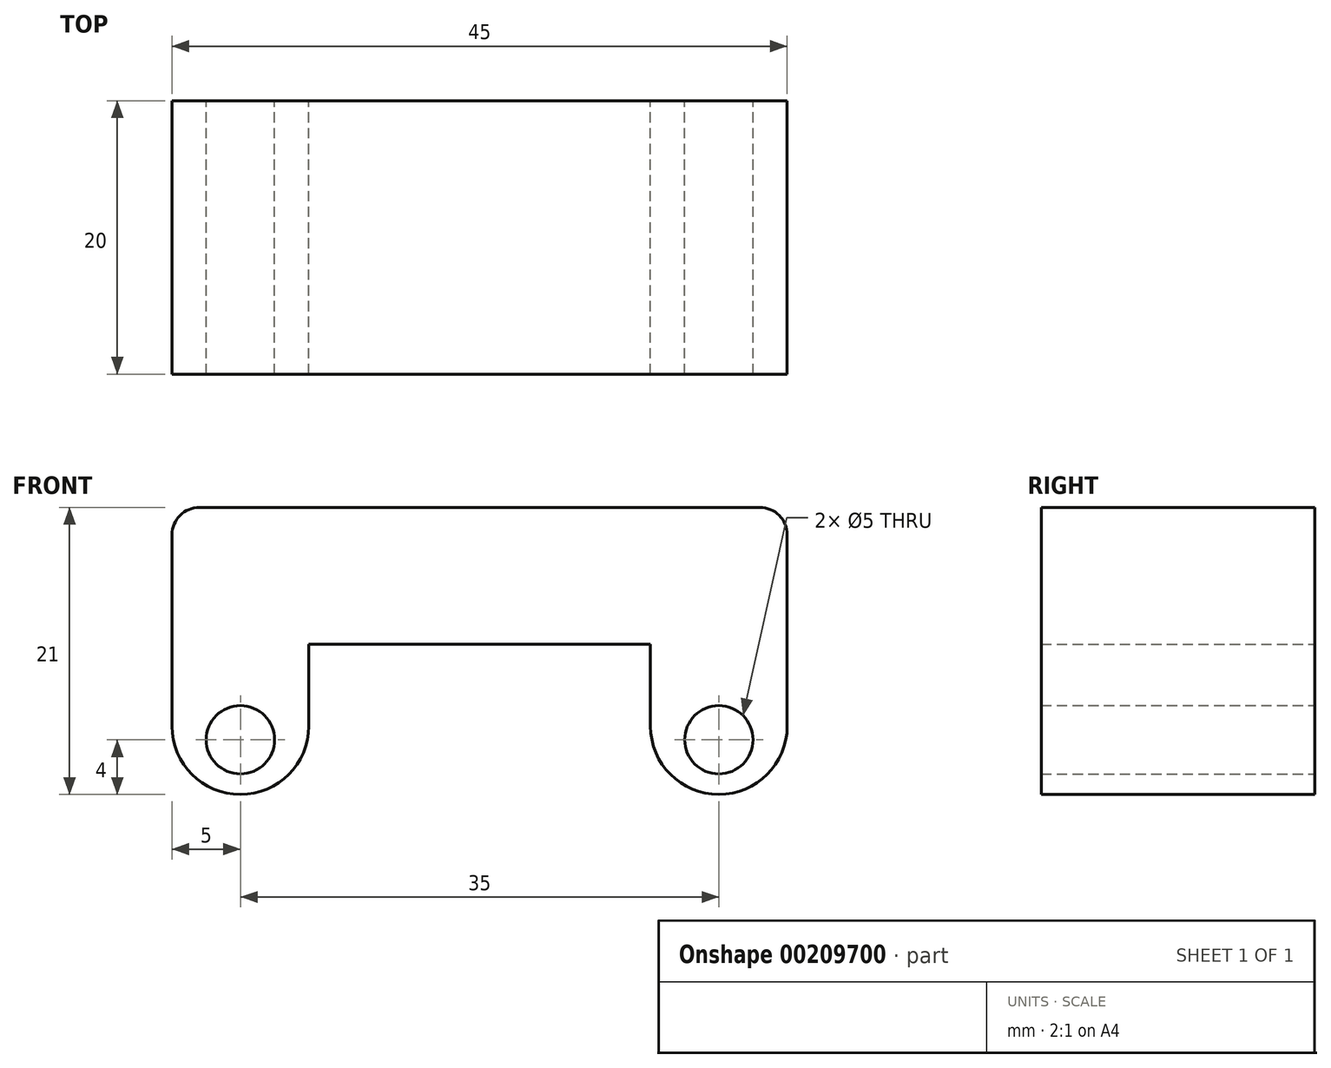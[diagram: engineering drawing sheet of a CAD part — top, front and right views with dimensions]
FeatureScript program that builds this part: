
annotation { "Feature Type Name" : "Feature", "Feature Type Description" : "" }
export const myFeature = defineFeature(function(context is Context, id is Id, definition is map)
    precondition{}
    {
        {
            var Q0;
            Q0=qCreatedBy(makeId("Front.planeOp"),FACE);
            var sketch = newSketch(context, id + "F0", { "sketchPlane" : qUnion([Q0])});
            skLineSegment(sketch, "E0.bottom", {"start": v(-22.5, 10.5) * mm, "end": v(22.5, 10.5) * mm});
            skLineSegment(sketch, "E0.top", {"start": v(-22.5, -10.5) * mm, "end": v(22.5, -10.5) * mm});
            skLineSegment(sketch, "E0.left", {"start": v(-22.5, 10.5) * mm, "end": v(-22.5, -10.5) * mm});
            skLineSegment(sketch, "E0.right", {"start": v(22.5, 10.5) * mm, "end": v(22.5, -10.5) * mm});
            skPoint(sketch, "E0.middle", {"position": v(0, 0) * mm});
            skCircle(sketch, "E1", {"center": v(-17.5, -6.5) * mm, "radius": 2.5 * mm});
            skLineSegment(sketch, "E2.bottom", {"start": v(-12.5, -10.5) * mm, "end": v(12.5, -10.5) * mm});
            skLineSegment(sketch, "E2.top", {"start": v(-12.5, 0.5) * mm, "end": v(12.5, 0.5) * mm});
            skLineSegment(sketch, "E2.left", {"start": v(-12.5, -10.5) * mm, "end": v(-12.5, 0.5) * mm});
            skLineSegment(sketch, "E2.right", {"start": v(12.5, -10.5) * mm, "end": v(12.5, 0.5) * mm});
            skCircle(sketch, "E3", {"center": v(17.5, -6.5) * mm, "radius": 2.5 * mm});
            skSolve(sketch);
        }
        {
            var Q0;
            Q0=makeQuery(id+"F0.imprint","IMPRINT",FACE,{"disambiguationData":[TD([[makeQuery(id+"F0.imprint","IMPRINT",EDGE,{"derivedFrom":sQuery(id+"F0.wireOp",EDGE,"E0.bottom")}),-1.0]])]});
            extrude(context, id + "F1", {"entities" : qUnion([Q0]), "depth" : 20 * mm});
        }
        {
            var Q0;
            Q0=makeQuery(id+"F1.opExtrude","SWEPT_EDGE",EDGE,{"disambiguationData":[OSD([sQuery(id+"F0.wireOp",EDGE,"E0.top"),sQuery(id+"F0.wireOp",EDGE,"E0.left")])]});
            var Q1;
            Q1=makeQuery(id+"F1.opExtrude","SWEPT_EDGE",EDGE,{"disambiguationData":[OSD([sQuery(id+"F0.wireOp",EDGE,"E0.top"),sQuery(id+"F0.wireOp",EDGE,"E2.bottom"),sQuery(id+"F0.wireOp",EDGE,"E2.left")])]});
            var Q2;
            Q2=makeQuery(id+"F1.opExtrude","SWEPT_EDGE",EDGE,{"disambiguationData":[OSD([sQuery(id+"F0.wireOp",EDGE,"E0.top"),sQuery(id+"F0.wireOp",EDGE,"E2.bottom"),sQuery(id+"F0.wireOp",EDGE,"E2.right")])]});
            var Q3;
            Q3=makeQuery(id+"F1.opExtrude","SWEPT_EDGE",EDGE,{"disambiguationData":[OSD([sQuery(id+"F0.wireOp",EDGE,"E0.top"),sQuery(id+"F0.wireOp",EDGE,"E0.right")])]});
            fillet(context, id + "F2", {"entities" : qUnion([Q0, Q1, Q2, Q3]), "radius" : 5 * mm, "tangentPropagation" : true, "allowEdgeOverflow" : false});
        }
        {
            var Q0;
            Q0=makeQuery(id+"F1.opExtrude","SWEPT_EDGE",EDGE,{"disambiguationData":[OSD([sQuery(id+"F0.wireOp",EDGE,"E0.bottom"),sQuery(id+"F0.wireOp",EDGE,"E0.right")])]});
            var Q1;
            Q1=makeQuery(id+"F1.opExtrude","SWEPT_EDGE",EDGE,{"disambiguationData":[OSD([sQuery(id+"F0.wireOp",EDGE,"E0.bottom"),sQuery(id+"F0.wireOp",EDGE,"E0.left")])]});
            fillet(context, id + "F3", {"entities" : qUnion([Q0, Q1]), "radius" : 2 * mm, "tangentPropagation" : true, "allowEdgeOverflow" : false});
        }
    });
